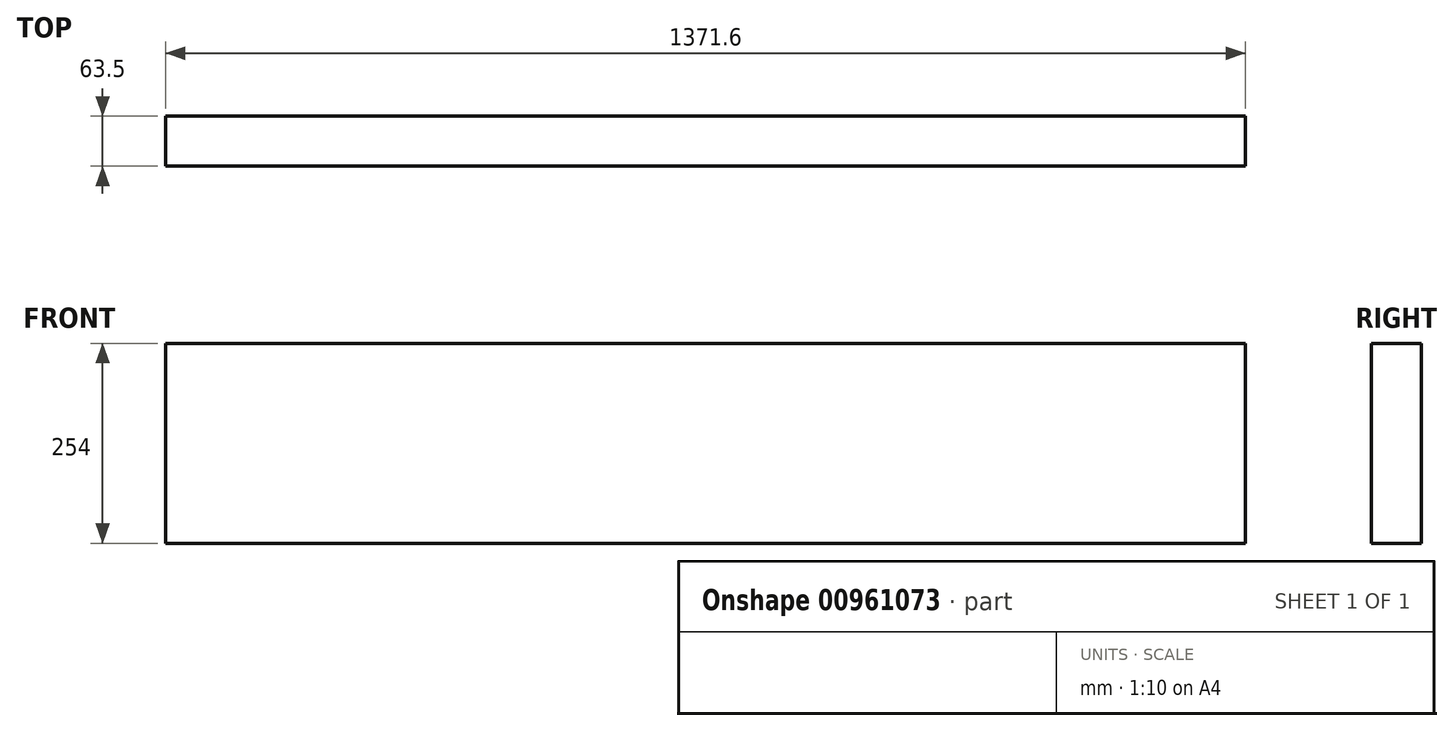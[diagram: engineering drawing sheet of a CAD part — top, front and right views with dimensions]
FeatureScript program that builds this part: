
annotation { "Feature Type Name" : "Feature", "Feature Type Description" : "" }
export const myFeature = defineFeature(function(context is Context, id is Id, definition is map)
    precondition{}
    {
        {
            var Q0;
            Q0=qCreatedBy(makeId("Front.planeOp"),FACE);
            var sketch = newSketch(context, id + "F0", { "sketchPlane" : qUnion([Q0])});
            skLineSegment(sketch, "E0.bottom", {"start": v(-691.5, 159.25) * mm, "end": v(680.1, 159.25) * mm});
            skLineSegment(sketch, "E0.top", {"start": v(-691.5, -94.75) * mm, "end": v(680.1, -94.75) * mm});
            skLineSegment(sketch, "E0.left", {"start": v(-691.5, 159.25) * mm, "end": v(-691.5, -94.75) * mm});
            skLineSegment(sketch, "E0.right", {"start": v(680.1, 159.25) * mm, "end": v(680.1, -94.75) * mm});
            skSolve(sketch);
        }
        {
            var Q0;
            Q0=makeQuery(id+"F0.imprint","IMPRINT",FACE,{"disambiguationData":[TD([[makeQuery(id+"F0.imprint","IMPRINT",EDGE,{"derivedFrom":sQuery(id+"F0.wireOp",EDGE,"E0.bottom")}),-1.0]])]});
            extrude(context, id + "F1", {"entities" : qUnion([Q0]), "depth" : 63.5 * mm, "offsetDistance" : 25.4 * mm});
        }
    });
